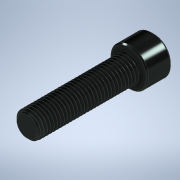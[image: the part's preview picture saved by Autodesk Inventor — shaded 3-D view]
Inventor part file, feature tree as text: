
AUTODESK INVENTOR PART (.ipt)
format: ipt  version: 2020 (Build 240168000, 168)  size: 997,376 bytes
history: native  units: in
note: dims shown in document units (in); Inventor stores cm internally (conversion verified against a paired STEP export)
features: chamfer x1
ambient origin geometry x8: Origin, YZ Plane, XZ Plane, XY Plane, X Axis, Y Axis, Z Axis, Center Point
bodies: Solid1 (feature_tree)
feature tree (1):
  chamfer  "Chamfer2"  [1 undecoded]
note: 1 required parameter value undecoded (feature->parameter linkage not recoverable at this tier; creation-order binding heuristic only, values carry confidence <= 0.55)
